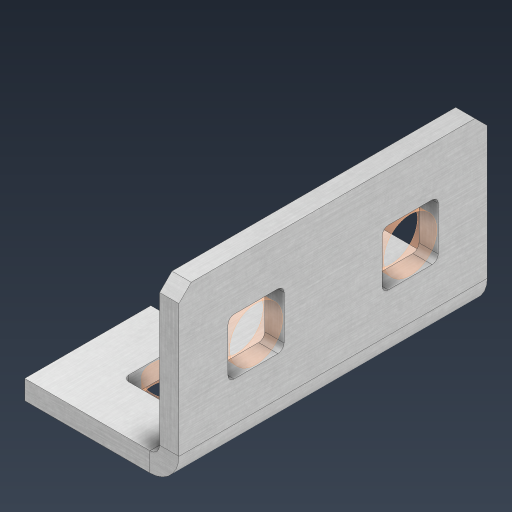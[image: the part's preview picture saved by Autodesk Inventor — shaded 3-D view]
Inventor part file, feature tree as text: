
AUTODESK INVENTOR PART (.ipt)
format: ipt  version: 2024.3 (Build 283343000, 343)  size: 448,000 bytes
history: native  units: in
note: dims shown in document units (in); Inventor stores cm internally (conversion verified against a paired STEP export)
features: other x13, sheet_metal_op x11, extrude x4, pattern_linear x2, mirror x1, chamfer x1, sketch x1
ambient origin geometry x8: Origin, YZ Plane, XZ Plane, XY Plane, X Axis, Y Axis, Z Axis, Center Point
bodies: Solid1 (feature_tree), Body (feature_tree)
feature tree (33):
  sheet_metal_op  "Flanges"
  other  "Flange Pattern Plane"
  other  "Flange Pattern Sketch"
  sheet_metal_op  "Flange Pattern"
  sheet_metal_op  "Body Pattern"
  pattern_linear  "Center Pattern"  Spacing1=1.0in  [1 undecoded]
  other  "Arc Length"
  mirror  "Notch Mirror"
  pattern_linear  "Notch Pattern"  Spacing1=0.0625in  [1 undecoded]
  chamfer  "End Chamfer"
  extrude  "Half Cut"  Depth=0.0625in
  other  "Plate1"
  sketch  "Sketch2"  dims[d0=1.0in d1=1.0in d2=0.0625in d3=0.0625in d4=0.0312in d5=0.125in d6=0.0625in d7=0.5in d8=90.0deg d9=0.0312in d10=0.25in d11=0.0625in d12=0.0625in d16=0.182in d17=0.02in d18=0.0625in d19=0.0in d20=0.25in d21=0.25in d38=0.7874in d40=0.5in d41=0.3937in d43=1.0in d46=0.172in d47=1.0in d48=0.0in d49=0.182in d50=0.02in d51=0.25in d52=0.25in d53=0.0625in d54=0.0in d55=0.172in d56=1.0in d57=0.0in d58=0.25in d60=0.7874in d62=0.5in d63=0.3937in d65=0.5in d85=0.1473in d86=0.1782in d88=0.04in d89=0.0625in d90=0.0in d91=0.04in d92=0.0491in d95=2.5in d96=0.04in d97=0.25in d98=45.0deg d99=0.25in d100=0.5in d101=0.0in d102=2.497in d106=0.182in d107=0.02in d108=0.5in d109=0.5in d110=0.0625in d111=0.0in d112=0.172in d113=0.5in d114=0.0in d117=0.5in d118=0.5in d119=0.5in]
  other  "Plate2"
  sheet_metal_op  "Bend1"
  sheet_metal_op  "Corner1"
  other  "Srf1"
  other  "Srf2"
  other  "Srf91"
  sheet_metal_op  "Body Pattern Sketch"
  other  "Srf92"
  other  "Srf786"
  other  "Srf889"
  sheet_metal_op  "Flange Stamp"
  sheet_metal_op  "Flange Circle"
  sheet_metal_op  "Body Stamp"
  sheet_metal_op  "Body Circle"
  other  "Center Stamp"
  other  "Center Circle"
  sheet_metal_op  "Notch"
  extrude  "ExtrusionSrf2"  Depth=0.0312in
  extrude  "ExtrusionSrf92"  Depth=0.5in
  extrude  "ExtrusionSrf889"  Depth=0.0625in
note: 2 required parameter values undecoded (feature->parameter linkage not recoverable at this tier; creation-order binding heuristic only, values carry confidence <= 0.55)
